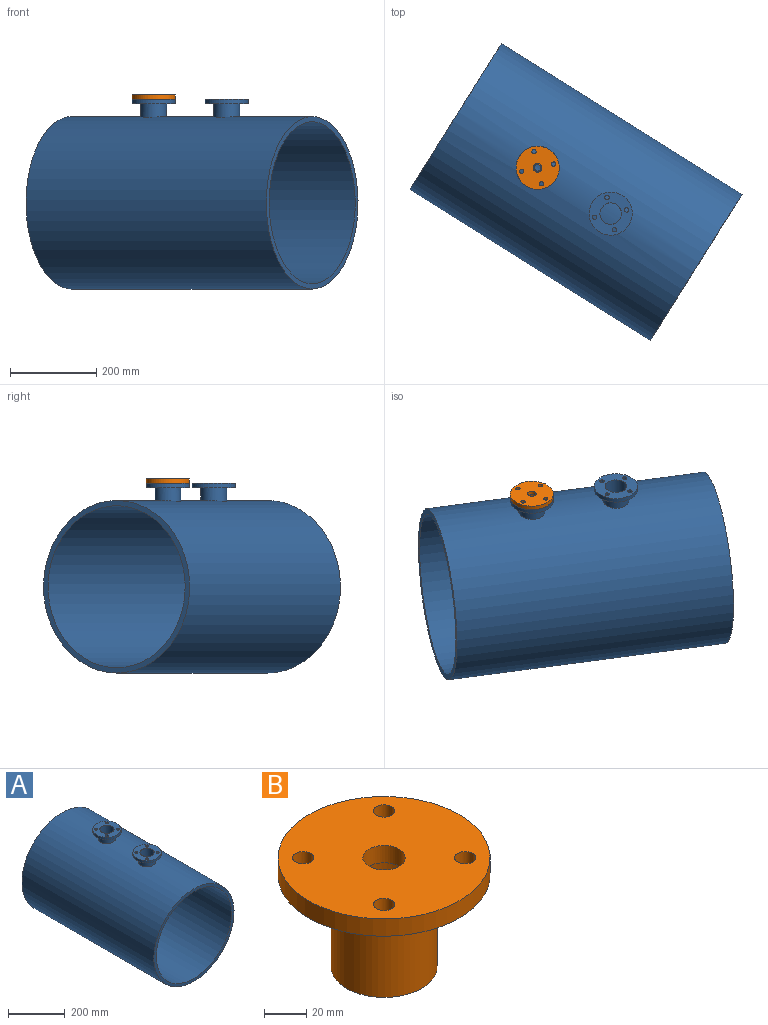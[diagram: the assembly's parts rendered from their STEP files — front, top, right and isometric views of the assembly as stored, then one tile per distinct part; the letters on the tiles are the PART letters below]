
ASSEMBLY  parts=2 mates=1
PART A: 23 faces, bbox 400x658x440 mm
  f0: cylinder r=187.7mm len=658mm, axis (0,1,0), area 774044.4mm2, adj f2,f3,f22
  f1: cylinder r=200mm len=658mm, axis (0,1,0), area 821192mm2, adj f2,f3,f4,f5
  f2: plane 400x400mm, normal (0,-1,0), area 14981.3mm2, adj f0,f1
  f3: plane 400x400mm, normal (0,1,0), area 14981.3mm2, adj f0,f1
  f4: cylinder r=30mm len=60mm, axis (0,0,1), area 5867.6mm2, adj f1,f9
  f5: cylinder r=30mm len=60mm, axis (0,0,1), area 5867.6mm2, adj f1,f6
  f6: plane 100x100mm, normal (0,0,-1), area 4712.4mm2, adj f5,f8,f16,f17,f18,f19
  f7: plane 100x100mm, normal (0,0,1), area 5576.3mm2, adj f8,f16,f17,f18,f19,f21
  f8: cylinder r=50mm len=100mm, axis (0,0,-1), area 3141.6mm2, adj f6,f7
  f9: plane 100x100mm, normal (0,0,-1), area 4712.4mm2, adj f4,f11,f12,f13,f14,f15
  f10: plane 100x100mm, normal (0,0,1), area 5576.3mm2, adj f11,f12,f13,f14,f15,f22
  f11: cylinder r=50mm len=100mm, axis (0,0,-1), area 3141.6mm2, adj f9,f10
  f12: cylinder r=5mm len=10mm, axis (0,0,1), area 314.2mm2, adj f9,f10
  f13: cylinder r=5mm len=10mm, axis (0,0,1), area 314.2mm2, adj f9,f10
  f14: cylinder r=5mm len=10mm, axis (0,0,1), area 314.2mm2, adj f9,f10
  f15: cylinder r=5mm len=10mm, axis (0,0,1), area 314.2mm2, adj f9,f10
  f16: cylinder r=5mm len=10mm, axis (0,0,1), area 314.2mm2, adj f6,f7
  f17: cylinder r=5mm len=10mm, axis (0,0,1), area 314.2mm2, adj f6,f7
  f18: cylinder r=5mm len=10mm, axis (0,0,1), area 314.2mm2, adj f6,f7
  f19: cylinder r=5mm len=10mm, axis (0,0,1), area 314.2mm2, adj f6,f7
  f20: cylinder r=200mm len=50mm, axis (0,1,0), area 1967.4mm2, adj f21
  f21: cylinder r=25mm len=50mm, axis (0,0,1), area 6406.3mm2, adj f7,f20
  f22: cylinder r=25mm len=53.97mm, axis (0,0,1), area 8346.3mm2, adj f0,f10
PART B: 14 faces, bbox 100x100x63 mm
  f0: cylinder r=50mm len=100mm, axis (0,0,-1), area 3141.6mm2, adj f1,f2
  f1: plane 100x100mm, normal (0,0,1), area 7225.7mm2, adj f0,f4,f5,f6,f7,f8
  f2: plane 100x100mm, normal (0,0,-1), area 5576.3mm2, adj f0,f3,f5,f6,f7,f8
  f3: cylinder r=25mm len=53mm, axis (0,0,1), area 8325.2mm2, adj f2,f12
  f4: cylinder r=10mm len=20mm, axis (0,0,1), area 628.3mm2, adj f1,f9
  f5: cylinder r=5mm len=10mm, axis (0,0,1), area 314.2mm2, adj f1,f2
  f6: cylinder r=5mm len=10mm, axis (0,0,1), area 314.2mm2, adj f1,f2
  f7: cylinder r=5mm len=10mm, axis (0,0,1), area 314.2mm2, adj f1,f2
  f8: cylinder r=5mm len=10mm, axis (0,0,1), area 314.2mm2, adj f1,f2
  f9: plane 40x40mm, normal (0,0,-1), area 942.5mm2, adj f4,f10
  f10: cylinder r=20mm len=43mm, axis (0,0,-1), area 5403.5mm2, adj f9,f11
  f11: plane 40x40mm, normal (0,0,1), area 1079.9mm2, adj f10,f13
  f12: plane 50x50mm, normal (0,0,-1), area 1786.8mm2, adj f3,f13
  f13: cylinder r=7.5mm len=15mm, axis (0,0,-1), area 471.2mm2, adj f11,f12
PLACE A rot(axis=(0,0,1),57.9deg) t=(-147.61,224.99,62.7)mm
PLACE B rot(axis=(0,0,1),147.9deg) t=(42.14,105.96,302.7)mm
MATE revolute B.f3 <-> A.f4  axis (0,0,1) through (42.14,105.96,302.7)mm
